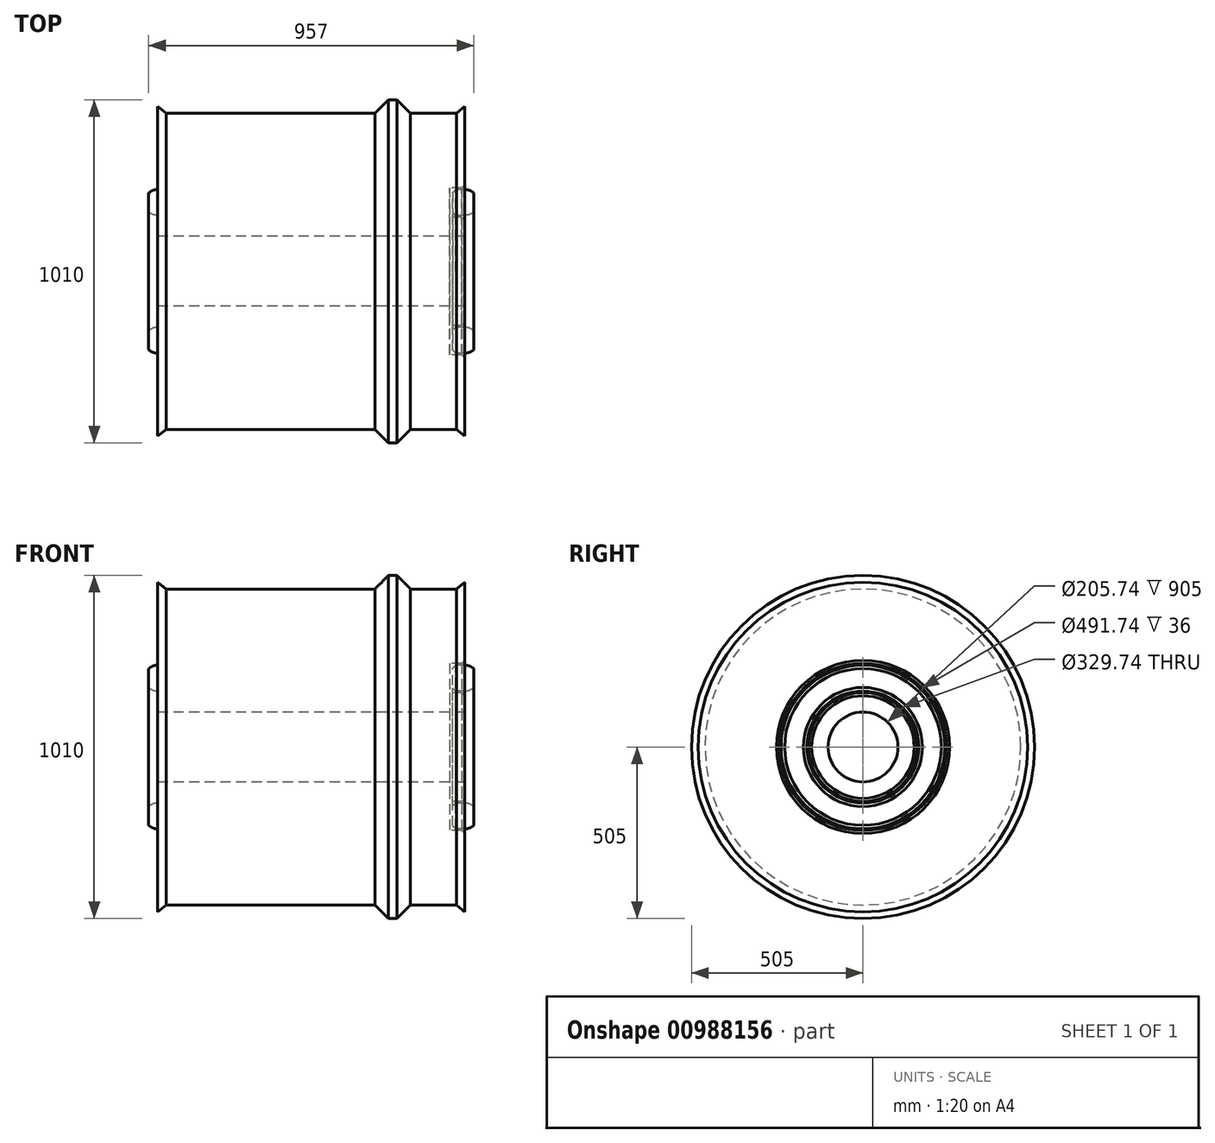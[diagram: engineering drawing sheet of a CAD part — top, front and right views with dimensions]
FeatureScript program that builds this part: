
annotation { "Feature Type Name" : "Feature", "Feature Type Description" : "" }
export const myFeature = defineFeature(function(context is Context, id is Id, definition is map)
    precondition{}
    {
        {
            var Q0;
            Q0=qCreatedBy(makeId("Top.planeOp"),FACE);
            var sketch = newSketch(context, id + "F0", { "sketchPlane" : qUnion([Q0])});
            skLineSegment(sketch, "E0", {"start": v(0, 102.87) * mm, "end": v(905, 102.87) * mm});
            skLineSegment(sketch, "E1", {"start": v(0, 0) * mm, "end": v(704.78, 0) * mm, "construction": true});
            skLineSegment(sketch, "E2", {"start": v(25, 465) * mm, "end": v(640, 465) * mm});
            skLineSegment(sketch, "E3", {"start": v(640, 465) * mm, "end": v(680, 505) * mm});
            skLineSegment(sketch, "E4", {"start": v(680, 505) * mm, "end": v(705, 505) * mm});
            skLineSegment(sketch, "E5", {"start": v(705, 505) * mm, "end": v(745, 465) * mm});
            skLineSegment(sketch, "E6.trimOffspring", {"start": v(745, 465) * mm, "end": v(880, 465) * mm});
            skLineSegment(sketch, "E7", {"start": v(0, 465) * mm, "end": v(0, 240.87) * mm});
            skLineSegment(sketch, "E8", {"start": v(905, 102.87) * mm, "end": v(905, 159.87) * mm});
            skLineSegment(sketch, "E9", {"start": v(25, 465) * mm, "end": v(0, 485) * mm});
            skLineSegment(sketch, "E10", {"start": v(0, 485) * mm, "end": v(0, 465) * mm});
            skLineSegment(sketch, "E11", {"start": v(905, 465) * mm, "end": v(905, 485) * mm});
            skLineSegment(sketch, "E12", {"start": v(905, 485) * mm, "end": v(880, 465) * mm});
            skArc(sketch, "E13", {"start": v(0, 164.87) * mm, "mid": v(-13.98, 167.54) * mm, "end": v(-26, 175.16) * mm});
            skLineSegment(sketch, "E14", {"start": v(-26, 230.58) * mm, "end": v(-26, 175.16) * mm});
            skArc(sketch, "E15.trimOffspring", {"start": v(-26, 230.58) * mm, "mid": v(-13.98, 238.2) * mm, "end": v(0, 240.87) * mm});
            skArc(sketch, "E16", {"start": v(0, 240.87) * mm, "mid": v(-38, 202.87) * mm, "end": v(0, 164.87) * mm, "construction": true});
            skLineSegment(sketch, "E17.trimOffspring", {"start": v(0, 164.87) * mm, "end": v(0, 102.87) * mm});
            skLineSegment(sketch, "E18", {"start": v(905, 245.87) * mm, "end": v(860, 245.87) * mm});
            skLineSegment(sketch, "E19", {"start": v(860, 245.87) * mm, "end": v(860, 159.87) * mm});
            skLineSegment(sketch, "E20", {"start": v(860, 159.87) * mm, "end": v(905, 159.87) * mm});
            skLineSegment(sketch, "E21", {"start": v(860, 202.87) * mm, "end": v(0, 202.87) * mm, "construction": true});
            skLineSegment(sketch, "E22.trimOffspring", {"start": v(905, 245.87) * mm, "end": v(905, 465) * mm});
            skLineSegment(sketch, "E23.bottom", {"start": v(869, 240.87) * mm, "end": v(905, 240.87) * mm});
            skLineSegment(sketch, "E23.top", {"start": v(869, 164.87) * mm, "end": v(905, 164.87) * mm});
            skLineSegment(sketch, "E23.left", {"start": v(869, 240.87) * mm, "end": v(869, 164.87) * mm});
            skLineSegment(sketch, "E23.right", {"start": v(905, 240.87) * mm, "end": v(905, 164.87) * mm, "construction": true});
            skArc(sketch, "E24", {"start": v(905, 164.87) * mm, "mid": v(918.98, 167.54) * mm, "end": v(931, 175.16) * mm});
            skLineSegment(sketch, "E25", {"start": v(905, 202.87) * mm, "end": v(860, 202.87) * mm, "construction": true});
            skLineSegment(sketch, "E26", {"start": v(931, 230.58) * mm, "end": v(931, 175.16) * mm});
            skArc(sketch, "E27.trimOffspring", {"start": v(931, 230.58) * mm, "mid": v(918.98, 238.2) * mm, "end": v(905, 240.87) * mm});
            skArc(sketch, "E28", {"start": v(905, 240.87) * mm, "mid": v(943, 202.87) * mm, "end": v(905, 164.87) * mm, "construction": true});
            skSolve(sketch);
        }
        {
            var Q0;
            Q0=makeQuery(id+"F0.imprint","IMPRINT",FACE,{"disambiguationData":[TD([[makeQuery(id+"F0.imprint","IMPRINT",EDGE,{"derivedFrom":sQuery(id+"F0.wireOp",EDGE,"E0")}),1.0]])]});
            var Q1;
            Q1=makeQuery(id+"F0.imprint","IMPRINT",FACE,{"disambiguationData":[TD([[makeQuery(id+"F0.imprint","IMPRINT",EDGE,{"derivedFrom":sQuery(id+"F0.wireOp",EDGE,"E23.bottom")}),-1.0]])]});
            var Q2;
            Q2=sQuery(id+"F0.wireOp",EDGE,"E1");
            revolve(context, id + "F1", {"surfaceOperationType" : NewSurfaceOperationType.NEW, "entities" : qUnion([Q0, Q1]), "axis" : qUnion([Q2]), "revolveType" : RevolveType.FULL});
        }
        {
            var Q0;
            Q0=makeQuery(id+"F1.opRevolve","SWEPT_EDGE",EDGE,{"disambiguationData":[OSD([sQuery(id+"F0.wireOp",EDGE,"E18"),sQuery(id+"F0.wireOp",EDGE,"E22.trimOffspring")])]});
            var Q1;
            Q1=makeQuery(id+"F1.opRevolve","SWEPT_EDGE",EDGE,{"disambiguationData":[OSD([sQuery(id+"F0.wireOp",EDGE,"E8"),sQuery(id+"F0.wireOp",EDGE,"E20")])]});
            var Q2;
            Q2=makeQuery(id+"F1.opRevolve","SWEPT_EDGE",EDGE,{"disambiguationData":[OSD([sQuery(id+"F0.wireOp",EDGE,"E23.bottom"),sQuery(id+"F0.wireOp",EDGE,"E23.left")])]});
            var Q3;
            Q3=makeQuery(id+"F1.opRevolve","SWEPT_EDGE",EDGE,{"disambiguationData":[OSD([sQuery(id+"F0.wireOp",EDGE,"E23.top"),sQuery(id+"F0.wireOp",EDGE,"E23.left")])]});
            chamfer(context, id + "F2", {"entities" : qUnion([Q0, Q1, Q2, Q3]), "width" : 9 * mm, "tangentPropagation" : true});
        }
    });
